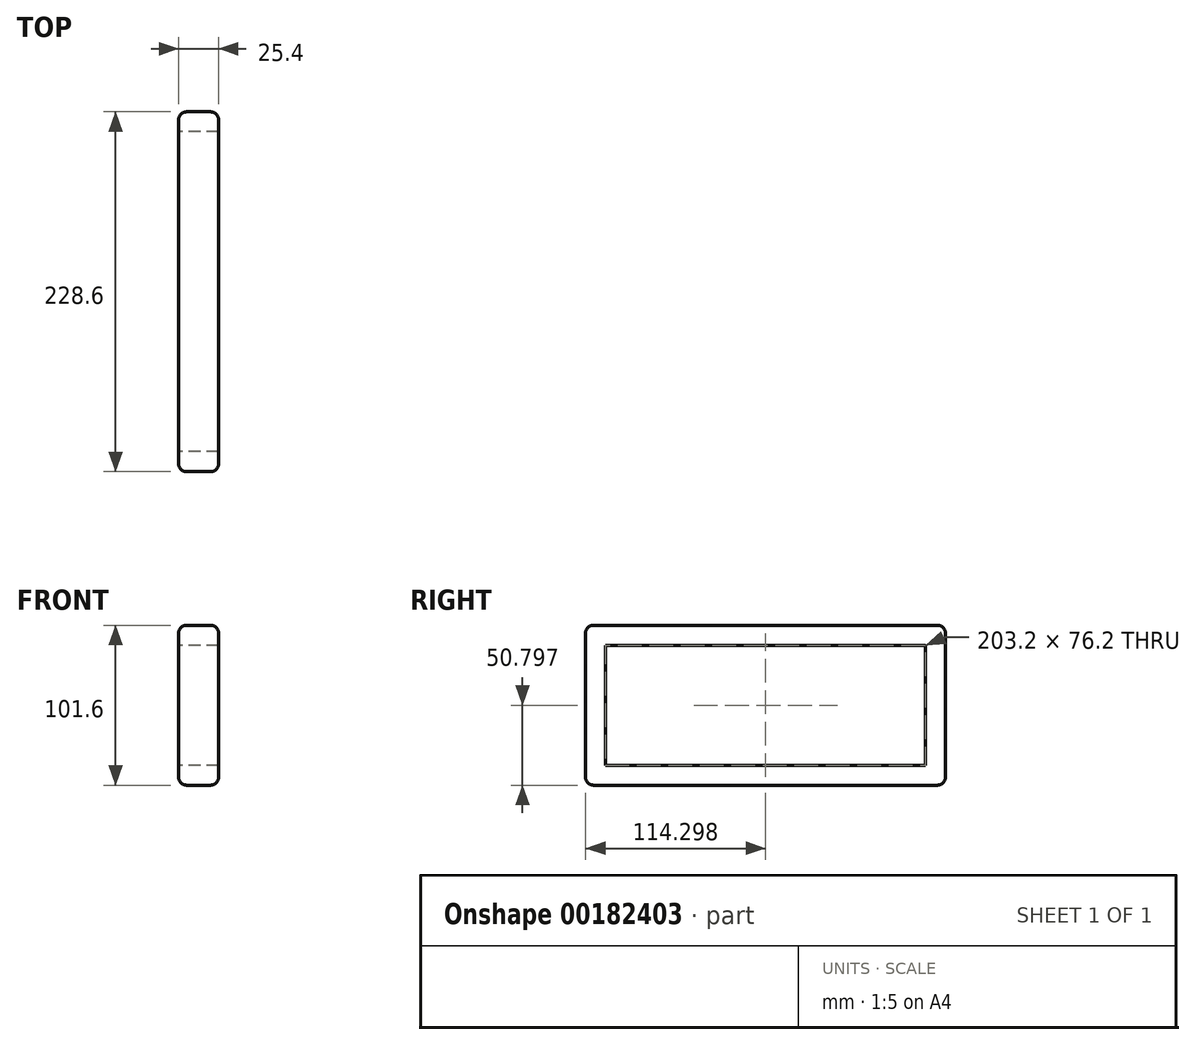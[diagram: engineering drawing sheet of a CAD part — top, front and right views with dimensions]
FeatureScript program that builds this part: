
annotation { "Feature Type Name" : "Feature", "Feature Type Description" : "" }
export const myFeature = defineFeature(function(context is Context, id is Id, definition is map)
    precondition{}
    {
        {
            var Q0;
            Q0=qCreatedBy(makeId("Right.planeOp"),FACE);
            var sketch = newSketch(context, id + "F0", { "sketchPlane" : qUnion([Q0])});
            skLineSegment(sketch, "E0.bottom", {"start": v(-113.82, 33.46) * mm, "end": v(114.78, 33.46) * mm});
            skLineSegment(sketch, "E0.top", {"start": v(-113.82, -68.14) * mm, "end": v(114.78, -68.14) * mm});
            skLineSegment(sketch, "E0.left", {"start": v(-113.82, 33.46) * mm, "end": v(-113.82, -68.14) * mm});
            skLineSegment(sketch, "E0.right", {"start": v(114.78, 33.46) * mm, "end": v(114.78, -68.14) * mm});
            skLineSegment(sketch, "E1.bottom", {"start": v(-101.12, 20.76) * mm, "end": v(102.08, 20.76) * mm});
            skLineSegment(sketch, "E1.top", {"start": v(-101.12, -55.44) * mm, "end": v(102.08, -55.44) * mm});
            skLineSegment(sketch, "E1.left", {"start": v(-101.12, 20.76) * mm, "end": v(-101.12, -55.44) * mm});
            skLineSegment(sketch, "E1.right", {"start": v(102.08, 20.76) * mm, "end": v(102.08, -55.44) * mm});
            skSolve(sketch);
        }
        {
            var Q0;
            Q0=makeQuery(id+"F0.imprint","IMPRINT",FACE,{"disambiguationData":[TD([[makeQuery(id+"F0.imprint","IMPRINT",EDGE,{"derivedFrom":sQuery(id+"F0.wireOp",EDGE,"E0.bottom")}),-1.0]])]});
            extrude(context, id + "F1", {"entities" : qUnion([Q0]), "depth" : 25.4 * mm});
        }
        {
            var Q0;
            Q0=makeQuery(id+"F1.opExtrude","SWEPT_FACE",FACE,{"disambiguationData":[OSD([sQuery(id+"F0.wireOp",EDGE,"E0.left")])]});
            var Q1;
            Q1=makeQuery(id+"F1.opExtrude","SWEPT_FACE",FACE,{"disambiguationData":[OSD([sQuery(id+"F0.wireOp",EDGE,"E0.right")])]});
            fillet(context, id + "F2", {"entities" : qUnion([Q0, Q1]), "radius" : 5.08 * mm, "tangentPropagation" : true, "allowEdgeOverflow" : false});
        }
        {
            var Q0;
            Q0=makeQuery(id+"F1.opExtrude","SWEPT_FACE",FACE,{"disambiguationData":[OSD([sQuery(id+"F0.wireOp",EDGE,"E0.top")])]});
            fillet(context, id + "F3", {"entities" : qUnion([Q0]), "radius" : 5.08 * mm, "tangentPropagation" : true, "allowEdgeOverflow" : false});
        }
        {
            var Q0;
            Q0=makeQuery(id+"F1.opExtrude","SWEPT_FACE",FACE,{"disambiguationData":[OSD([sQuery(id+"F0.wireOp",EDGE,"E0.bottom")])]});
            fillet(context, id + "F4", {"entities" : qUnion([Q0]), "radius" : 5.08 * mm, "tangentPropagation" : true, "allowEdgeOverflow" : false});
        }
    });
